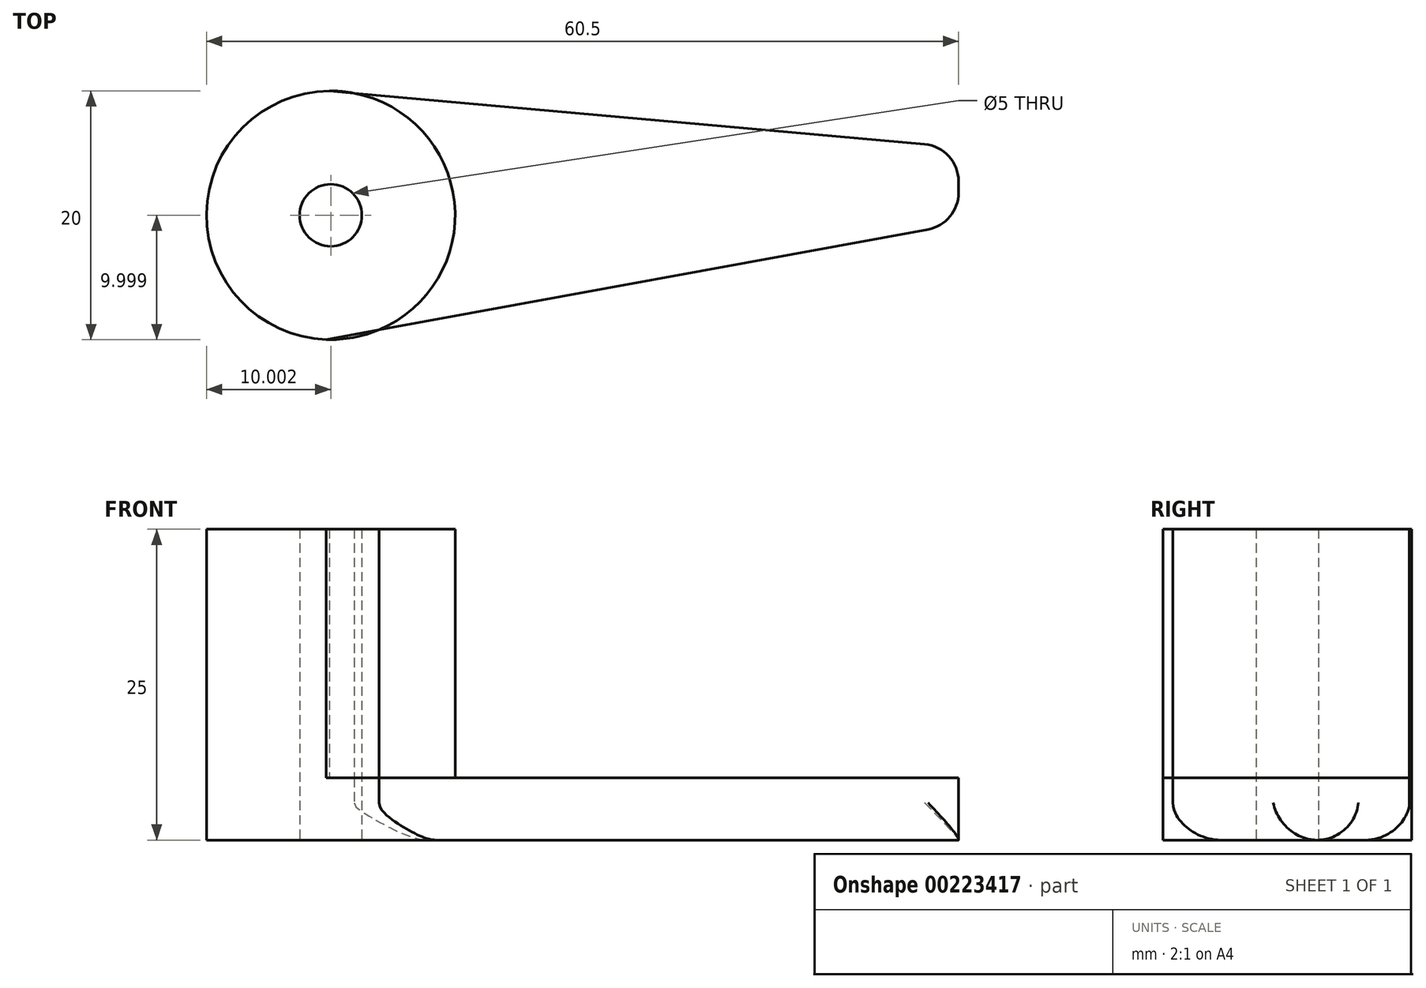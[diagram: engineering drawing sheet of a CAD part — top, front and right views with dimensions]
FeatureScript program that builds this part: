
annotation { "Feature Type Name" : "Feature", "Feature Type Description" : "" }
export const myFeature = defineFeature(function(context is Context, id is Id, definition is map)
    precondition{}
    {
        {
            var Q0;
            Q0=qCreatedBy(makeId("Top.planeOp"),FACE);
            var sketch = newSketch(context, id + "F0", { "sketchPlane" : qUnion([Q0])});
            skCircle(sketch, "E0", {"center": v(-50.5, 46.65) * mm, "radius": 10 * mm});
            skCircle(sketch, "E1", {"center": v(-50.5, 46.65) * mm, "radius": 2.5 * mm});
            skLineSegment(sketch, "E2", {"start": v(-50.6, 56.65) * mm, "end": v(0, 52.11) * mm});
            skLineSegment(sketch, "E3", {"start": v(0, 52.11) * mm, "end": v(0, 45.96) * mm});
            skLineSegment(sketch, "E4", {"start": v(0, 45.96) * mm, "end": v(-50.86, 36.66) * mm});
            skSolve(sketch);
        }
        {
            var Q0;
            Q0=makeQuery(id+"F0.imprint","IMPRINT",FACE,{"disambiguationData":[TD([[makeQuery(id+"F0.imprint","IMPRINT",EDGE,{"derivedFrom":sQuery(id+"F0.wireOp",EDGE,"E1")}),-1.0]])]});
            extrude(context, id + "F1", {"entities" : qUnion([Q0]), "depth" : 25 * mm});
        }
        {
            var Q0;
            Q0 = qSketchRegion(id + "F0", true);
            extrude(context, id + "F2", {"entities" : qUnion([Q0]), "operationType" : NewBodyOperationType.ADD, "depth" : 5 * mm});
        }
        {
            var Q0;
            Q0=makeQuery(id+"F2.opExtrude","SWEPT_EDGE",EDGE,{"disambiguationData":[OSD([sQuery(id+"F0.wireOp",EDGE,"E3"),sQuery(id+"F0.wireOp",EDGE,"E4")])]});
            var Q1;
            Q1=makeQuery(id+"F2.opExtrude","SWEPT_EDGE",EDGE,{"disambiguationData":[OSD([sQuery(id+"F0.wireOp",EDGE,"E2"),sQuery(id+"F0.wireOp",EDGE,"E3")])]});
            var Q2;
            Q2=makeQuery(id+"F2.opExtrude","CAP_EDGE",EDGE,{"disambiguationData":[OSD([sQuery(id+"F0.wireOp",EDGE,"E4")])],"isStart":true});
            var Q3;
            Q3=makeQuery(id+"F2.opExtrude","CAP_EDGE",EDGE,{"disambiguationData":[OSD([sQuery(id+"F0.wireOp",EDGE,"E2")])],"isStart":true});
            fillet(context, id + "F3", {"entities" : qUnion([Q0, Q1, Q2, Q3]), "radius" : 3 * mm, "tangentPropagation" : true, "allowEdgeOverflow" : false});
        }
    });
